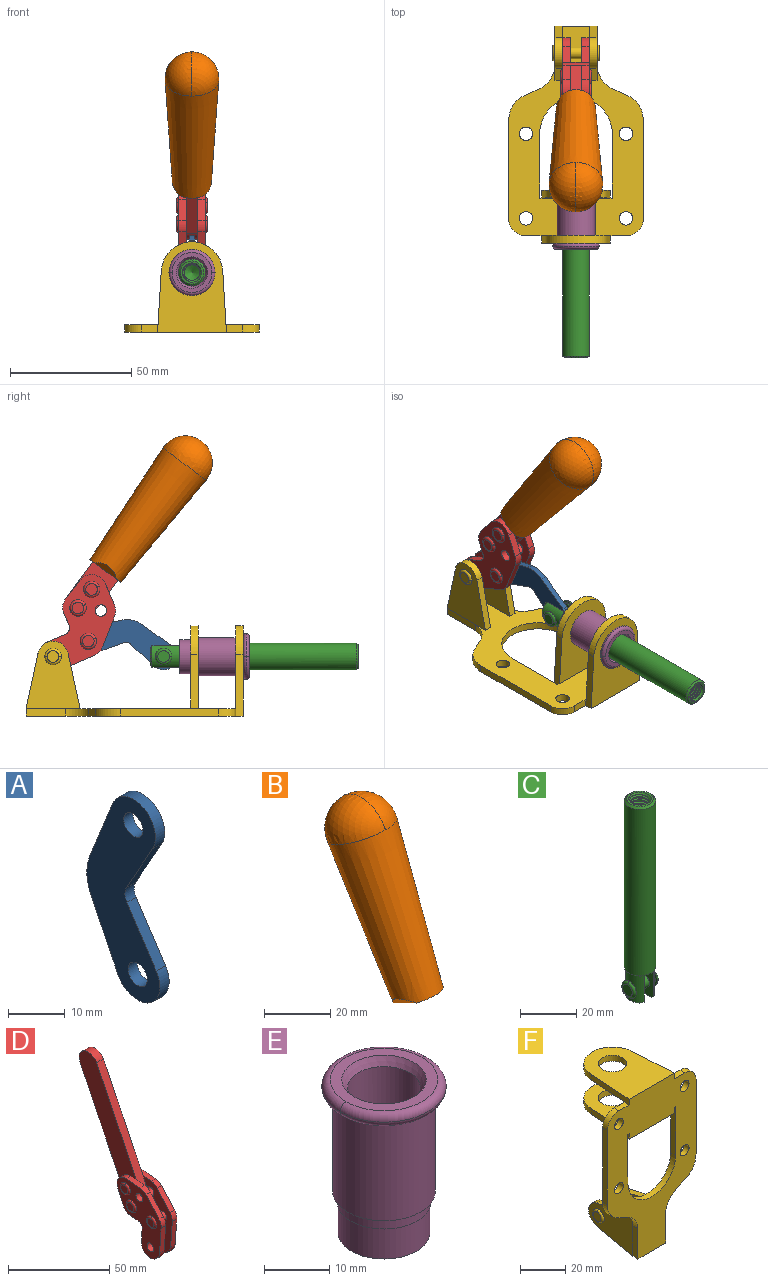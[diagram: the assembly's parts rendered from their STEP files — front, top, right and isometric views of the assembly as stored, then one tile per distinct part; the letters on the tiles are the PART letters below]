
ASSEMBLY  parts=6 mates=6
PART A: 12 faces, bbox 2.3x18.2x42.8 mm
  f0: cylinder r=2.4mm len=4.8mm, axis (1,0,0), area 34.9mm2, adj f4,f11
  f1: cylinder r=10.41mm len=8.47mm, axis (1,0,0), area 20.2mm2, adj f4,f9,f10,f11
  f2: cylinder r=3.05mm len=3.16mm, axis (1,0,0), area 7.7mm2, adj f4,f6,f7,f11
  f3: cylinder r=2.4mm len=4.8mm, axis (1,0,0), area 34.9mm2, adj f4,f11
  f4: plane 42.81x18.23mm, normal (-1,0,0), area 414.1mm2, adj f0,f1,f2,f3,f5,f6,f7,f8
  f5: cylinder r=5.54mm len=10.67mm, axis (1,0,0), area 41.8mm2, adj f4,f6,f10,f11
  f6: plane 11.66x6.53mm, normal (0,-0.87,-0.49), area 30.9mm2, adj f2,f4,f5,f11
  f7: plane 11.17x7.33mm, normal (0,-0.84,0.55), area 30.9mm2, adj f2,f4,f8,f11
  f8: cylinder r=5.54mm len=10.51mm, axis (1,0,0), area 41.8mm2, adj f4,f7,f9,f11
  f9: plane 13.67x6.67mm, normal (0,0.9,-0.44), area 35.1mm2, adj f1,f4,f8,f11
  f10: plane 14.1x5.7mm, normal (0,0.93,0.37), area 35.1mm2, adj f1,f4,f5,f11
  f11: plane 42.81x18.23mm, normal (1,0,0), area 414.1mm2, adj f0,f1,f2,f3,f5,f6,f7,f8
PART B: 11 faces, bbox 22.3x42.6x64.5 mm
  f0: sphere r=11.13mm, area 411.4mm2, adj f1,f8
  f1: cone r=11.11mm half-angle=3.3deg, axis (0,0.44,0.9), area 3251.8mm2, adj f0,f7,f8,f9,f10
  f2: cylinder r=6.16mm len=11.7mm, axis (1,0,0), area 89.5mm2, adj f3,f4,f5,f6
  f3: plane 60.23x36.75mm, normal (-1,0,0), area 763.6mm2, adj f2,f4,f6,f10
  f4: plane 51.37x25.05mm, normal (0,0.9,-0.44), area 264.2mm2, adj f2,f3,f5,f10
  f5: plane 60.23x36.75mm, normal (1,0,0), area 763.6mm2, adj f2,f4,f6,f10
  f6: plane 51.37x25.05mm, normal (0,-0.9,0.44), area 264.2mm2, adj f2,f3,f5,f10
  f7: plane 9.95x5.95mm, normal (0.71,-0.31,-0.64), area 25.8mm2, adj f1,f10
  f8: sphere r=11.13mm, area 411.4mm2, adj f0,f1
  f9: plane 9.95x5.95mm, normal (-0.71,-0.31,-0.64), area 25.8mm2, adj f1,f10
  f10: plane 14.27x11.38mm, normal (0,-0.44,-0.9), area 106.7mm2, adj f1,f3,f4,f5,f6,f7,f9
PART C: 48 faces, bbox 12.6x11.1x86.1 mm
  f0: torus R=2.41mm, axis (-1,0,0), area 15mm2, adj f30,f32,f34
  f1: torus R=2.41mm, axis (-1,0,0), area 15mm2, adj f29,f31,f33
  f2: cylinder r=5.54mm len=72.39mm, axis (0,0,1), area 2518.5mm2, adj f3,f4,f42,f43
  f3: cone r=5.54mm half-angle=45deg, axis (0,0,1), area 7.6mm2, adj f2,f5,f41
  f4: cone r=5.54mm half-angle=45deg, axis (0,0,-1), area 34.9mm2, adj f2,f39
  f5: cylinder r=5.08mm len=11.48mm, axis (0,0,1), area 108.3mm2, adj f3,f7,f8,f41
  f6: cylinder r=2.41mm len=4.83mm, axis (-1,0,0), area 71.2mm2, adj f40,f41
  f7: cylinder r=2.41mm len=4.83mm, axis (-1,0,0), area 7.6mm2, adj f5,f34
  f8: cone r=5.08mm half-angle=45deg, axis (0,0,1), area 10.6mm2, adj f5,f37,f41
  f9: cone r=3.98mm half-angle=45deg, axis (0,0,1), area 17.6mm2, adj f27,f39,f45,f46,f47
  f10: cylinder r=2.41mm len=4.83mm, axis (-1,0,0), area 7.6mm2, adj f33,f38
  f11: cylinder r=3.2mm len=6.4mm, axis (0,0,1), area 78.4mm2, adj f12,f28,f44,f45,f47
  f12: cylinder r=3.2mm len=6.4mm, axis (0,0,1), area 10.5mm2, adj f11,f13,f45,f47
  f13: cylinder r=3.2mm len=6.4mm, axis (0,0,1), area 10.5mm2, adj f12,f14,f45,f47
  f14: cylinder r=3.2mm len=6.4mm, axis (0,0,1), area 10.5mm2, adj f13,f15,f45,f47
  f15: cylinder r=3.2mm len=6.4mm, axis (0,0,1), area 10.5mm2, adj f14,f16,f45,f47
  f16: cylinder r=3.2mm len=6.4mm, axis (0,0,1), area 10.5mm2, adj f15,f17,f45,f47
  f17: cylinder r=3.2mm len=6.4mm, axis (0,0,1), area 10.5mm2, adj f16,f18,f45,f47
  f18: cylinder r=3.2mm len=6.4mm, axis (0,0,1), area 10.5mm2, adj f17,f19,f45,f47
  f19: cylinder r=3.2mm len=6.4mm, axis (0,0,1), area 10.5mm2, adj f18,f20,f45,f47
  f20: cylinder r=3.2mm len=6.4mm, axis (0,0,1), area 10.5mm2, adj f19,f21,f45,f47
  f21: cylinder r=3.2mm len=6.4mm, axis (0,0,1), area 10.5mm2, adj f20,f22,f45,f47
  f22: cylinder r=3.2mm len=6.4mm, axis (0,0,1), area 10.5mm2, adj f21,f23,f45,f47
  f23: cylinder r=3.2mm len=6.4mm, axis (0,0,1), area 10.5mm2, adj f22,f24,f45,f47
  f24: cylinder r=3.2mm len=6.4mm, axis (0,0,1), area 10.5mm2, adj f23,f25,f45,f47
  f25: cylinder r=3.2mm len=6.4mm, axis (0,0,1), area 10.5mm2, adj f24,f26,f45,f47
  f26: cylinder r=3.2mm len=6.4mm, axis (0,0,1), area 10.5mm2, adj f25,f27,f45,f47
  f27: cylinder r=3.2mm len=6.4mm, axis (0,0,1), area 7.4mm2, adj f9,f26,f45,f47
  f28: cone r=3.2mm half-angle=60deg, axis (0,0,1), area 37.2mm2, adj f11
  f29: plane 4.83x4.83mm, normal (-1,0,0), area 18.3mm2, adj f1,f31
  f30: plane 4.83x4.83mm, normal (1,0,0), area 18.3mm2, adj f0,f32
  f31: torus R=2.41mm, axis (-1,0,0), area 15mm2, adj f1,f29,f33
  f32: torus R=2.41mm, axis (-1,0,0), area 15mm2, adj f0,f30,f34
  f33: plane 6.83x6.83mm, normal (1,0,0), area 18.3mm2, adj f1,f10,f31
  f34: plane 6.83x6.83mm, normal (-1,0,0), area 18.3mm2, adj f0,f7,f32
  f35: cone r=5.08mm half-angle=45deg, axis (0,0,1), area 10.6mm2, adj f36,f38,f40
  f36: plane 7.25x1.97mm, normal (0,0,-1), area 10mm2, adj f35,f40
  f37: plane 7.25x1.97mm, normal (0,0,-1), area 10mm2, adj f8,f41
  f38: cylinder r=5.08mm len=11.48mm, axis (0,0,1), area 108.3mm2, adj f10,f35,f40,f42
  f39: plane 9.55x9.55mm, normal (0,0,1), area 22mm2, adj f4,f9
  f40: plane 12.76x10.09mm, normal (1,0,0), area 95.7mm2, adj f6,f35,f36,f38,f42,f43
  f41: plane 12.76x10.09mm, normal (-1,0,0), area 95.7mm2, adj f3,f5,f6,f8,f37,f43
  f42: cone r=5.54mm half-angle=45deg, axis (0,0,1), area 7.6mm2, adj f2,f38,f40
  f43: plane 11.07x4.7mm, normal (0,0,-1), area 50.4mm2, adj f2,f40,f41
  f44: plane 0.89x0.62mm, normal (-1,0,0), area 0.3mm2, adj f11,f45,f46,f47
  f45: bspline ~24.8x7.63mm, area 266.6mm2, adj f9,f11,f12,f13,f14,f15,f16,f17
  f46: bspline ~24.87x7.63mm, area 73.6mm2, adj f9,f44,f45,f47
  f47: bspline ~24.98x7.63mm, area 272.5mm2, adj f9,f11,f12,f13,f14,f15,f16,f17
PART D: 59 faces, bbox 12.9x60.2x99.6 mm
  f0: torus R=2.39mm, axis (-1,0,0), area 14.9mm2, adj f20,f43,f51
  f1: torus R=2.39mm, axis (-1,0,0), area 14.9mm2, adj f19,f42,f51
  f2: torus R=2.39mm, axis (-1,0,0), area 14.9mm2, adj f18,f35,f51
  f3: torus R=2.39mm, axis (-1,0,0), area 14.9mm2, adj f14,f17,f23
  f4: torus R=2.39mm, axis (-1,0,0), area 14.9mm2, adj f13,f16,f23
  f5: torus R=2.39mm, axis (-1,0,0), area 14.9mm2, adj f12,f15,f23
  f6: cylinder r=2.39mm len=4.78mm, axis (1,0,0), area 46.5mm2, adj f48,f50,f51
  f7: cylinder r=2.39mm len=4.78mm, axis (1,0,0), area 46.5mm2, adj f50,f51
  f8: cylinder r=6.35mm len=12.68mm, axis (1,0,0), area 61.8mm2, adj f38,f39,f50,f51
  f9: cylinder r=2.39mm len=4.78mm, axis (-1,0,0), area 70.5mm2, adj f46,f50
  f10: cylinder r=2.39mm len=4.78mm, axis (-1,0,0), area 46.5mm2, adj f23,f45,f46
  f11: cylinder r=2.39mm len=4.78mm, axis (-1,0,0), area 46.5mm2, adj f23,f46
  f12: plane 4.78x4.78mm, normal (1,0,0), area 17.9mm2, adj f5,f15
  f13: plane 4.78x4.78mm, normal (1,0,0), area 17.9mm2, adj f4,f16
  f14: plane 4.78x4.78mm, normal (1,0,0), area 17.9mm2, adj f3,f17
  f15: torus R=2.39mm, axis (-1,0,0), area 14.9mm2, adj f5,f12,f23
  f16: torus R=2.39mm, axis (-1,0,0), area 14.9mm2, adj f4,f13,f23
  f17: torus R=2.39mm, axis (-1,0,0), area 14.9mm2, adj f3,f14,f23
  f18: plane 4.78x4.78mm, normal (-1,0,0), area 17.9mm2, adj f2,f35
  f19: plane 4.78x4.78mm, normal (-1,0,0), area 17.9mm2, adj f1,f42
  f20: plane 4.78x4.78mm, normal (-1,0,0), area 17.9mm2, adj f0,f43
  f21: plane 2.26x0.2mm, normal (1,0,0), area 0.2mm2, adj f31,f44
  f22: plane 2.26x0.2mm, normal (-1,0,0), area 0.2mm2, adj f41,f44
  f23: plane 39.37x30.77mm, normal (1,0,0), area 565.5mm2, adj f3,f4,f5,f10,f11,f15,f16,f17
  f24: cylinder r=6.1mm len=4.15mm, axis (-1,0,0), area 14.7mm2, adj f23,f25,f32,f46
  f25: plane 10.25x9.01mm, normal (0,-0.75,0.66), area 42.3mm2, adj f23,f24,f26,f46
  f26: cylinder r=6.35mm len=4.64mm, axis (-1,0,0), area 15.6mm2, adj f23,f25,f27,f46
  f27: plane 15.84x3.1mm, normal (0,-1,-0.07), area 49.2mm2, adj f23,f26,f28,f46
  f28: cylinder r=6.35mm len=12.68mm, axis (-1,0,0), area 61.8mm2, adj f23,f27,f29,f46
  f29: plane 8.11x3.1mm, normal (0,1,0.07), area 25.2mm2, adj f23,f28,f30,f46
  f30: cylinder r=3.05mm len=3.25mm, axis (-1,0,0), area 14.8mm2, adj f23,f29,f31,f46
  f31: plane 5.99x3.1mm, normal (0,0.07,-1), area 18.6mm2, adj f21,f23,f30,f44,f46
  f32: plane 9.5x3.1mm, normal (0,-0.07,1), area 29.5mm2, adj f23,f24,f33,f46,f47
  f33: cylinder r=6.1mm len=8.63mm, axis (-1,0,0), area 39.1mm2, adj f23,f32,f34,f47
  f34: plane 8.65x3.96mm, normal (0,0.91,-0.42), area 29.5mm2, adj f23,f33,f44,f47
  f35: torus R=2.39mm, axis (-1,0,0), area 14.9mm2, adj f2,f18,f51
  f36: plane 10.25x9.01mm, normal (0,-0.75,0.66), area 42.3mm2, adj f37,f49,f50,f51
  f37: cylinder r=6.35mm len=4.64mm, axis (1,0,0), area 15.6mm2, adj f36,f38,f50,f51
  f38: plane 15.84x3.1mm, normal (0,-1,-0.07), area 49.2mm2, adj f8,f37,f50,f51
  f39: plane 8.11x3.1mm, normal (0,1,0.07), area 25.2mm2, adj f8,f40,f50,f51
  f40: cylinder r=3.05mm len=3.25mm, axis (1,0,0), area 14.8mm2, adj f39,f41,f50,f51
  f41: plane 5.99x3.1mm, normal (0,0.07,-1), area 18.6mm2, adj f22,f40,f44,f50,f51
  f42: torus R=2.39mm, axis (-1,0,0), area 14.9mm2, adj f1,f19,f51
  f43: torus R=2.39mm, axis (-1,0,0), area 14.9mm2, adj f0,f20,f51
  f44: cylinder r=6.35mm len=12.12mm, axis (-1,0,0), area 128.9mm2, adj f21,f22,f23,f31,f34,f41,f46,f47
  f45: plane 2.65x1.35mm, normal (1,0,0), area 1mm2, adj f10,f55
  f46: plane 39.08x20.42mm, normal (-1,0,0), area 412.5mm2, adj f9,f10,f11,f24,f25,f26,f27,f28
  f47: plane 77.62x39.82mm, normal (1,0,0), area 850mm2, adj f32,f33,f34,f44,f53,f54,f55
  f48: plane 2.65x1.35mm, normal (-1,0,0), area 1mm2, adj f6,f55
  f49: cylinder r=6.1mm len=4.15mm, axis (1,0,0), area 14.7mm2, adj f36,f50,f51,f56
  f50: plane 39.08x20.42mm, normal (1,0,0), area 412.5mm2, adj f6,f7,f8,f9,f36,f37,f38,f39
  f51: plane 39.37x30.77mm, normal (-1,0,0), area 565.5mm2, adj f0,f1,f2,f6,f7,f8,f35,f36
  f52: plane 8.65x3.96mm, normal (0,0.91,-0.42), area 29.5mm2, adj f44,f51,f57,f58
  f53: plane 68.49x33.4mm, normal (0,0.9,-0.44), area 358.1mm2, adj f44,f47,f54,f58
  f54: cylinder r=6.35mm len=12.06mm, axis (1,0,0), area 93.7mm2, adj f47,f53,f55,f58
  f55: plane 68.49x33.4mm, normal (0,-0.9,0.44), area 358.1mm2, adj f44,f45,f46,f47,f48,f50,f54,f58
  f56: plane 9.5x3.1mm, normal (0,-0.07,1), area 29.5mm2, adj f49,f50,f51,f57,f58
  f57: cylinder r=6.1mm len=8.63mm, axis (1,0,0), area 39.1mm2, adj f51,f52,f56,f58
  f58: plane 77.62x39.82mm, normal (-1,0,0), area 850mm2, adj f44,f52,f53,f54,f55,f56,f57
PART E: 15 faces, bbox 20.6x20.6x28.7 mm
  f0: torus R=8.26mm, axis (0,0,1), area 56.8mm2, adj f1,f10,f12
  f1: torus R=8.26mm, axis (0,0,1), area 56.8mm2, adj f0,f6,f13
  f2: cylinder r=5.59mm len=25.91mm, axis (0,0,1), area 909.6mm2, adj f3,f4
  f3: cone r=6.86mm half-angle=45deg, axis (0,0,-1), area 70.2mm2, adj f2,f14
  f4: cone r=6.47mm half-angle=30deg, axis (0,0,1), area 66.7mm2, adj f2,f13
  f5: cylinder r=7.04mm len=14.07mm, axis (0,0,1), area 252.6mm2, adj f11,f14
  f6: torus R=8.26mm, axis (0,0,1), area 56.8mm2, adj f1,f12,f13
  f7: cylinder r=7.16mm len=14.33mm, axis (0,0,1), area 91.5mm2, adj f9,f11
  f8: cylinder r=7.86mm len=18.42mm, axis (0,0,1), area 909.6mm2, adj f9,f10
  f9: plane 15.72x15.72mm, normal (0,0,-1), area 33mm2, adj f7,f8
  f10: plane 16.51x16.51mm, normal (0,0,-1), area 19.9mm2, adj f0,f8,f12
  f11: plane 14.33x14.33mm, normal (0,0,-1), area 5.7mm2, adj f5,f7
  f12: torus R=8.26mm, axis (0,0,1), area 56.8mm2, adj f0,f6,f10
  f13: plane 16.51x16.51mm, normal (0,0,1), area 82.7mm2, adj f1,f4,f6
  f14: plane 14.07x14.07mm, normal (0,0,-1), area 7.8mm2, adj f3,f5
PART F: 55 faces, bbox 55.7x37.4x89.8 mm
  f0: torus R=2.41mm, axis (-1,0,0), area 15mm2, adj f11,f15,f25
  f1: torus R=2.41mm, axis (-1,0,0), area 15mm2, adj f10,f12,f22
  f2: cylinder r=2.78mm len=5.56mm, axis (0,-1,0), area 54.2mm2, adj f30,f54
  f3: cylinder r=14.99mm len=29.97mm, axis (0,-1,0), area 145.9mm2, adj f30,f49,f53,f54
  f4: cylinder r=2.78mm len=5.56mm, axis (0,-1,0), area 54.2mm2, adj f30,f54
  f5: cylinder r=2.78mm len=5.56mm, axis (0,-1,0), area 54.2mm2, adj f30,f54
  f6: cylinder r=2.78mm len=5.56mm, axis (0,-1,0), area 54.2mm2, adj f30,f54
  f7: cylinder r=6.35mm len=12.7mm, axis (0,0,1), area 123.6mm2, adj f27,f51
  f8: cylinder r=6.35mm len=12.7mm, axis (0,0,-1), area 124.7mm2, adj f21,f35
  f9: cylinder r=2.41mm len=11.18mm, axis (-1,0,0), area 169.4mm2, adj f16,f19
  f10: plane 4.83x4.83mm, normal (1,0,0), area 18.3mm2, adj f1,f12
  f11: plane 4.83x4.83mm, normal (-1,0,0), area 18.3mm2, adj f0,f15
  f12: torus R=2.41mm, axis (-1,0,0), area 15mm2, adj f1,f10,f22
  f13: cylinder r=6.35mm len=12.41mm, axis (1,0,0), area 53.4mm2, adj f18,f19,f22,f23
  f14: cylinder r=6.35mm len=12.41mm, axis (-1,0,0), area 53.4mm2, adj f16,f17,f24,f25
  f15: torus R=2.41mm, axis (-1,0,0), area 15mm2, adj f0,f11,f25
  f16: plane 27.86x22.35mm, normal (1,0,0), area 425.4mm2, adj f9,f14,f17,f24,f30
  f17: plane 22.86x4.97mm, normal (0,0.21,0.98), area 72.5mm2, adj f14,f16,f25,f30
  f18: plane 22.86x4.97mm, normal (0,0.21,0.98), area 72.5mm2, adj f13,f19,f22,f30
  f19: plane 27.86x22.35mm, normal (-1,0,0), area 425.4mm2, adj f9,f13,f18,f23,f30
  f20: cylinder r=12.7mm len=25.35mm, axis (0,0,-1), area 119.8mm2, adj f21,f34,f35,f36
  f21: plane 34.21x28.07mm, normal (0,0,-1), area 702.4mm2, adj f8,f20,f30,f34,f36
  f22: plane 27.96x22.45mm, normal (1,0,0), area 407.2mm2, adj f1,f12,f13,f18,f23,f30,f42,f43
  f23: plane 22.86x4.97mm, normal (0,0.21,-0.98), area 72.5mm2, adj f13,f19,f22,f44
  f24: plane 22.86x4.97mm, normal (0,0.21,-0.98), area 72.5mm2, adj f14,f16,f25,f44
  f25: plane 27.86x22.35mm, normal (-1,0,0), area 407.1mm2, adj f0,f14,f15,f17,f24,f30,f45,f46
  f26: plane 3.1x0.95mm, normal (0,0,-1), area 2.7mm2, adj f30,f49,f50,f54
  f27: plane 34.21x28.07mm, normal (0,0,1), area 702.4mm2, adj f7,f28,f30,f50,f52
  f28: cylinder r=12.7mm len=25.35mm, axis (0,0,1), area 118.8mm2, adj f27,f50,f51,f52
  f29: plane 3.1x0.95mm, normal (0,0,-1), area 2.7mm2, adj f30,f52,f53,f54
  f30: plane 86.54x55.63mm, normal (0,1,0), area 2362.9mm2, adj f2,f3,f4,f5,f6,f16,f17,f18
  f31: plane 40.56x3.1mm, normal (-1,0,0), area 125.7mm2, adj f30,f32,f48,f54
  f32: cylinder r=7.11mm len=7.11mm, axis (0,-1,0), area 34.6mm2, adj f30,f31,f33,f54
  f33: plane 6.67x3.1mm, normal (0,0,1), area 20.4mm2, adj f30,f32,f34,f54
  f34: plane 25.39x3.13mm, normal (-1,0.06,0), area 79.5mm2, adj f20,f21,f33,f35,f54
  f35: plane 37.31x28.45mm, normal (0,0,1), area 789.9mm2, adj f8,f20,f34,f36,f54
  f36: plane 25.39x3.13mm, normal (1,0.06,0), area 79.5mm2, adj f20,f21,f35,f37,f54
  f37: plane 6.67x3.1mm, normal (0,0,1), area 20.4mm2, adj f30,f36,f38,f54
  f38: cylinder r=7.11mm len=7.11mm, axis (0,-1,0), area 34.6mm2, adj f30,f37,f39,f54
  f39: plane 40.56x3.1mm, normal (1,0,0), area 125.7mm2, adj f30,f38,f40,f54
  f40: cylinder r=11.18mm len=10.16mm, axis (0,-1,0), area 39.5mm2, adj f30,f39,f41,f54
  f41: plane 6.09x3.1mm, normal (0.42,0,-0.91), area 20.8mm2, adj f30,f40,f42,f54
  f42: cylinder r=11.18mm len=9.41mm, axis (0,-1,0), area 37.2mm2, adj f22,f30,f41,f43,f54
  f43: plane 16.5x3.1mm, normal (1,0,0), area 51.1mm2, adj f22,f42,f44,f54
  f44: plane 17.37x3.1mm, normal (0,0,-1), area 53.8mm2, adj f23,f24,f30,f43,f45,f54
  f45: plane 16.5x3.1mm, normal (-1,0,0), area 51.1mm2, adj f25,f44,f46,f54
  f46: cylinder r=11.18mm len=9.41mm, axis (0,-1,0), area 37.2mm2, adj f25,f30,f45,f47,f54
  f47: plane 6.09x3.1mm, normal (-0.42,0,-0.91), area 20.8mm2, adj f30,f46,f48,f54
  f48: cylinder r=11.18mm len=10.16mm, axis (0,-1,0), area 39.5mm2, adj f30,f31,f47,f54
  f49: plane 26.54x3.1mm, normal (-1,0,0), area 82.3mm2, adj f3,f26,f30,f54
  f50: plane 25.39x3.1mm, normal (1,0.06,0), area 78.8mm2, adj f26,f27,f28,f51,f54
  f51: plane 37.31x28.45mm, normal (0,0,-1), area 789.9mm2, adj f7,f28,f50,f52,f54
  f52: plane 25.39x3.1mm, normal (-1,0.06,0), area 78.8mm2, adj f27,f28,f29,f51,f54
  f53: plane 26.54x3.1mm, normal (1,0,0), area 82.3mm2, adj f3,f29,f30,f54
  f54: plane 89.66x55.63mm, normal (0,-1,0), area 2678.5mm2, adj f2,f3,f4,f5,f6,f26,f29,f31
PLACE A rot(axis=(1,0,0),103.5deg) t=(0,16.36,4.29)mm
PLACE B rot(axis=(1,0,0),62.5deg) t=(-0.04,1.4,17.6)mm
PLACE C rot(axis=(1,0,0),90deg) t=(0,11.04,0)mm
PLACE D rot(axis=(1,0,0),62.5deg) t=(0,1.4,17.6)mm
PLACE E rot(axis=(1,0,0),90deg) t=(0,9.14,0)mm
PLACE F rot(axis=(1,0,0),90deg) t=(0,9.14,0)mm fixed
MATE fastened D.f54 <-> B.f2  axis (-1,0,0) through (-2.35,-14.38,105.91)mm
MATE revolute D.f7 <-> F.f0  axis (-1,0,0) through (0,41.23,24.61)mm
MATE slider C.f2 <-> E.f0  axis (0,-1,0) through (0,-47.74,24.61)mm
MATE revolute A.f3 <-> D.f4  axis (1,0,0) through (0,26.67,30.94)mm
MATE fastened F.f7 <-> E.f0  axis (0,1,0) through (0,-37.25,24.61)mm
MATE revolute C.f6 <-> A.f5  axis (-1,0,0) through (0,-4.44,24.61)mm
